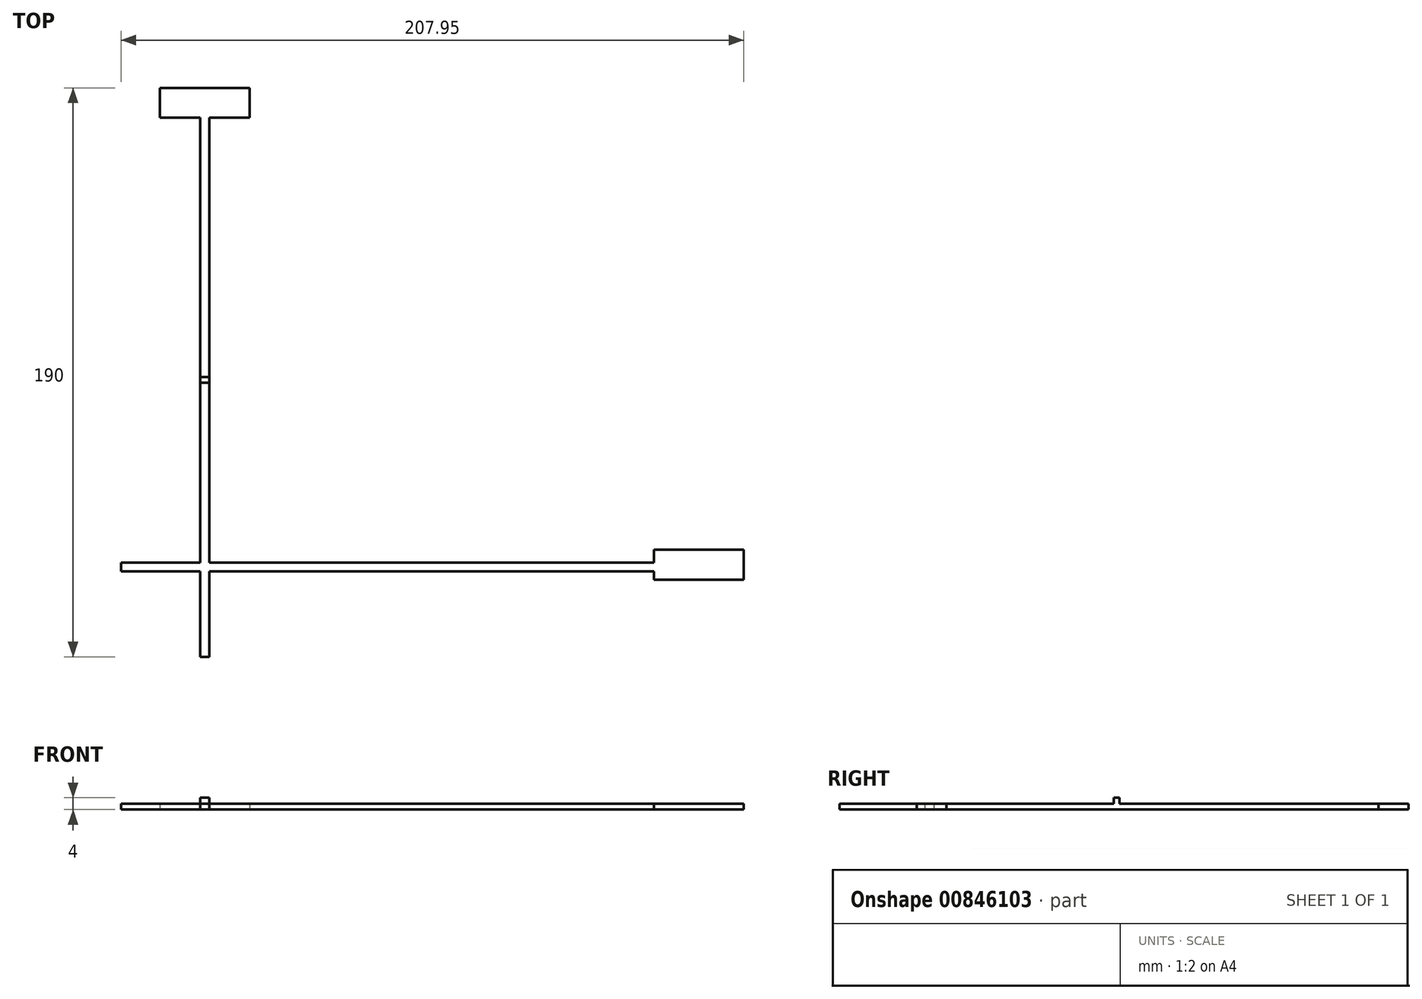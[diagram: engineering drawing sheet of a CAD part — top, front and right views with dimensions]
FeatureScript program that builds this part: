
annotation { "Feature Type Name" : "Feature", "Feature Type Description" : "" }
export const myFeature = defineFeature(function(context is Context, id is Id, definition is map)
    precondition{}
    {
        {
            var Q0;
            Q0=qCreatedBy(makeId("Top.planeOp"),FACE);
            var sketch = newSketch(context, id + "F0", { "sketchPlane" : qUnion([Q0])});
            skLineSegment(sketch, "E0.bottom", {"start": v(-27.95, 1.5) * mm, "end": v(152.05, 1.5) * mm});
            skLineSegment(sketch, "E0.top", {"start": v(-27.95, -1.5) * mm, "end": v(152.05, -1.5) * mm});
            skLineSegment(sketch, "E0.left", {"start": v(-27.95, 1.5) * mm, "end": v(-27.95, -1.5) * mm});
            skLineSegment(sketch, "E1.bottom", {"start": v(-1.5, 150) * mm, "end": v(1.5, 150) * mm});
            skLineSegment(sketch, "E1.top", {"start": v(-1.5, -30) * mm, "end": v(1.5, -30) * mm});
            skLineSegment(sketch, "E1.left", {"start": v(-1.5, 150) * mm, "end": v(-1.5, -30) * mm});
            skLineSegment(sketch, "E1.right", {"start": v(1.5, 150) * mm, "end": v(1.5, -30) * mm});
            skLineSegment(sketch, "E2.bottom", {"start": v(15, 150) * mm, "end": v(-15, 150) * mm});
            skLineSegment(sketch, "E2.top", {"start": v(15, 160) * mm, "end": v(-15, 160) * mm});
            skLineSegment(sketch, "E2.left", {"start": v(15, 150) * mm, "end": v(15, 160) * mm});
            skLineSegment(sketch, "E2.right", {"start": v(-15, 150) * mm, "end": v(-15, 160) * mm});
            skPoint(sketch, "E2.middle", {"position": v(0, 155) * mm});
            skPoint(sketch, "E3", {"position": v(0, 150) * mm});
            skLineSegment(sketch, "E4.bottom", {"start": v(180, -4.26) * mm, "end": v(150, -4.26) * mm});
            skLineSegment(sketch, "E4.top", {"start": v(180, 5.74) * mm, "end": v(150, 5.74) * mm});
            skLineSegment(sketch, "E4.left", {"start": v(180, -4.26) * mm, "end": v(180, 5.74) * mm});
            skLineSegment(sketch, "E4.right", {"start": v(150, -4.26) * mm, "end": v(150, 5.74) * mm});
            skPoint(sketch, "E5", {"position": v(150, 0) * mm});
            skPoint(sketch, "E6", {"position": v(0, 61.5) * mm});
            skPoint(sketch, "E7", {"position": v(31.5, 1.5) * mm});
            skPoint(sketch, "E8", {"position": v(91.5, 1.5) * mm});
            skPoint(sketch, "E9", {"position": v(121.5, 1.5) * mm});
            skLineSegment(sketch, "E10", {"start": v(0, 61.5) * mm, "end": v(31.77, 61.5) * mm});
            skFitSpline(sketch, "E11", {"points": [v(31.77, 61.5) * mm, v(48.5, 126.9) * mm, v(66.37, 44.61) * mm, v(82.07, 53.82) * mm, v(85.95, 57.97) * mm, v(89.59, 61.5) * mm, v(101.88, 61.5) * mm], "startDerivative": vector(68.12, 400.53) * mm, "endDerivative": vector(121.44, -15.97) * mm});
            skFitSpline(sketch, "E12.0", {"points": [v(29.8, 61.84) * mm, v(30.5, 66) * mm, v(31.92, 74.35) * mm, v(34.04, 86.49) * mm, v(35.77, 95.95) * mm, v(37.13, 102.95) * mm, v(38.14, 107.85) * mm, v(39.13, 112.37) * mm, v(40.1, 116.45) * mm, v(41.06, 120.06) * mm, v(41.84, 122.64) * mm, v(42.47, 124.44) * mm, v(42.94, 125.64) * mm, v(43.42, 126.72) * mm, v(43.91, 127.66) * mm, v(44.46, 128.49) * mm, v(45, 129.1) * mm, v(45.55, 129.54) * mm, v(46.05, 129.83) * mm, v(46.66, 130.03) * mm, v(47.36, 130.1) * mm, v(48.06, 129.97) * mm, v(48.67, 129.7) * mm, v(49.16, 129.34) * mm, v(49.68, 128.82) * mm, v(50.16, 128.1) * mm, v(50.61, 127.14) * mm, v(51, 126.05) * mm, v(51.38, 124.8) * mm, v(51.73, 123.4) * mm, v(52.18, 121.3) * mm, v(52.72, 118.32) * mm, v(53.35, 114.19) * mm, v(53.99, 109.6) * mm, v(54.63, 104.62) * mm, v(55.28, 99.36) * mm, v(56.2, 92.07) * mm, v(57.41, 82.66) * mm, v(58.8, 73.46) * mm, v(60.06, 66.6) * mm, v(61.07, 61.79) * mm, v(62.17, 57.4) * mm, v(63.35, 53.57) * mm, v(64.6, 50.37) * mm, v(65.7, 48.34) * mm, v(66.54, 47.16) * mm, v(67.05, 46.63) * mm, v(67.42, 46.32) * mm, v(67.76, 46.08) * mm, v(68.16, 45.89) * mm, v(68.64, 45.77) * mm, v(69.16, 45.75) * mm, v(69.76, 45.83) * mm, v(70.67, 46.1) * mm, v(71.97, 46.75) * mm, v(73.66, 47.97) * mm, v(75.37, 49.49) * mm, v(77.03, 51.16) * mm, v(78.57, 52.87) * mm, v(79.73, 54.2) * mm, v(80.57, 55.14) * mm, v(81.14, 55.78) * mm, v(81.66, 56.33) * mm, v(82.28, 56.98) * mm, v(82.94, 57.65) * mm, v(83.57, 58.3) * mm, v(84, 58.76) * mm, v(84.28, 59.1) * mm, v(84.44, 59.29) * mm, v(84.6, 59.51) * mm, v(84.84, 59.82) * mm, v(85.26, 60.37) * mm, v(85.88, 61.15) * mm, v(86.82, 62.11) * mm, v(87.73, 62.78) * mm, v(88.43, 63.17) * mm, v(88.93, 63.4) * mm, v(89.57, 63.65) * mm, v(90.37, 63.87) * mm, v(91.45, 64.08) * mm, v(92.86, 64.22) * mm, v(94.62, 64.23) * mm, v(96.45, 64.14) * mm, v(98.96, 63.9) * mm, v(100.88, 63.65) * mm, v(102.14, 63.48) * mm]});
            skLineSegment(sketch, "E12.1", {"start": v(0, 63.5) * mm, "end": v(30.08, 63.5) * mm});
            skLineSegment(sketch, "E13", {"start": v(102.14, 63.48) * mm, "end": v(101.88, 61.5) * mm});
            skLineSegment(sketch, "E14.bottom", {"start": v(1.5, 63.5) * mm, "end": v(-1.5, 63.5) * mm});
            skLineSegment(sketch, "E14.top", {"start": v(1.5, 61.5) * mm, "end": v(-1.5, 61.5) * mm});
            skLineSegment(sketch, "E14.left", {"start": v(1.5, 63.5) * mm, "end": v(1.5, 61.5) * mm});
            skLineSegment(sketch, "E14.right", {"start": v(-1.5, 63.5) * mm, "end": v(-1.5, 61.5) * mm});
            skSolve(sketch);
        }
        {
            var Q0;
            {var subQ1=sQuery(id+"F0.wireOp",EDGE,"E1.bottom");Q0=makeQuery(id+"F0.imprint","IMPRINT",FACE,{"disambiguationData":[TD([[makeQuery(id+"F0.imprint","IMPRINT",EDGE,{"derivedFrom":subQ1}),1.0]])]});}
            var Q1;
            {var subQ3=sQuery(id+"F0.wireOp",EDGE,"E14.top");Q1=makeQuery(id+"F0.imprint","IMPRINT",FACE,{"disambiguationData":[TD([[makeQuery(id+"F0.imprint","IMPRINT",EDGE,{"derivedFrom":subQ3}),1.0]])]});}
            var Q2;
            {var subQ0=sQuery(id+"F0.wireOp",EDGE,"E1.right");var subQ1=sQuery(id+"F0.wireOp",EDGE,"E0.bottom");var subQ2=makeQuery(id+"F0.imprint","INTERSECT",VERTEX,{"derivedFrom":[subQ1,subQ0]});Q2=makeQuery(id+"F0.imprint","IMPRINT",FACE,{"disambiguationData":[TD([[makeQuery(id+"F0.imprint","IMPRINT",EDGE,{"disambiguationData":[TD([[subQ2,-1.0]])],"derivedFrom":subQ1}),-1.0]])]});}
            var Q3;
            {var subQ0=sQuery(id+"F0.wireOp",EDGE,"E0.left");Q3=makeQuery(id+"F0.imprint","IMPRINT",FACE,{"disambiguationData":[TD([[makeQuery(id+"F0.imprint","IMPRINT",EDGE,{"derivedFrom":subQ0}),1.0]])]});}
            var Q4;
            {var subQ3=sQuery(id+"F0.wireOp",EDGE,"E4.bottom");Q4=makeQuery(id+"F0.imprint","IMPRINT",FACE,{"disambiguationData":[TD([[makeQuery(id+"F0.imprint","IMPRINT",EDGE,{"derivedFrom":subQ3}),-1.0]])]});}
            var Q5;
            {var subQ5=sQuery(id+"F0.wireOp",EDGE,"E1.top");Q5=makeQuery(id+"F0.imprint","IMPRINT",FACE,{"disambiguationData":[TD([[makeQuery(id+"F0.imprint","IMPRINT",EDGE,{"derivedFrom":subQ5}),1.0]])]});}
            var Q6;
            {var subQ0=sQuery(id+"F0.wireOp",EDGE,"E1.right");var subQ1=sQuery(id+"F0.wireOp",EDGE,"E0.bottom");var subQ2=makeQuery(id+"F0.imprint","INTERSECT",VERTEX,{"derivedFrom":[subQ1,subQ0]});Q6=makeQuery(id+"F0.imprint","IMPRINT",FACE,{"disambiguationData":[TD([[makeQuery(id+"F0.imprint","IMPRINT",EDGE,{"disambiguationData":[TD([[subQ2,1.0]])],"derivedFrom":subQ1}),-1.0]])]});}
            var Q7;
            {var subQ0=sQuery(id+"F0.wireOp",EDGE,"E0.right");Q7=makeQuery(id+"F0.imprint","IMPRINT",FACE,{"disambiguationData":[TD([[makeQuery(id+"F0.imprint","IMPRINT",EDGE,{"derivedFrom":subQ0}),-1.0]])]});}
            var Q8;
            {var subQ0=sQuery(id+"F0.wireOp",EDGE,"E1.right");var subQ1=sQuery(id+"F0.wireOp",EDGE,"E0.bottom");var subQ2=makeQuery(id+"F0.imprint","INTERSECT",VERTEX,{"derivedFrom":[subQ1,subQ0]});Q8=makeQuery(id+"F0.imprint","IMPRINT",FACE,{"disambiguationData":[TD([[makeQuery(id+"F0.imprint","IMPRINT",EDGE,{"disambiguationData":[TD([[subQ2,-1.0]])],"derivedFrom":subQ1}),-1.0]])]});}
            var Q9;
            {var subQ5=sQuery(id+"F0.wireOp",EDGE,"E1.bottom");Q9=makeQuery(id+"F0.imprint","IMPRINT",FACE,{"disambiguationData":[TD([[makeQuery(id+"F0.imprint","IMPRINT",EDGE,{"derivedFrom":subQ5}),-1.0]])]});}
            extrude(context, id + "F1", {"entities" : qUnion([Q0, Q1, Q2, Q3, Q4, Q5, Q6, Q7, Q8, Q9]), "depth" : 2 * mm, "offsetDistance" : 25 * mm});
        }
        {
            var Q0;
            {var subQ0=sQuery(id+"F0.wireOp",EDGE,"E11");Q0=makeQuery(id+"F0.imprint","IMPRINT",FACE,{"disambiguationData":[TD([[makeQuery(id+"F0.imprint","IMPRINT",EDGE,{"derivedFrom":subQ0}),1.0]])]});}
            var Q1;
            {var subQ3=sQuery(id+"F0.wireOp",EDGE,"E14.bottom");Q1=makeQuery(id+"F0.imprint","IMPRINT",FACE,{"disambiguationData":[TD([[makeQuery(id+"F0.imprint","IMPRINT",EDGE,{"derivedFrom":subQ3}),1.0]])]});}
            extrude(context, id + "F2", {"entities" : qUnion([Q0, Q1]), "operationType" : NewBodyOperationType.ADD, "depth" : 4 * mm, "offsetDistance" : 25 * mm});
        }
    });
